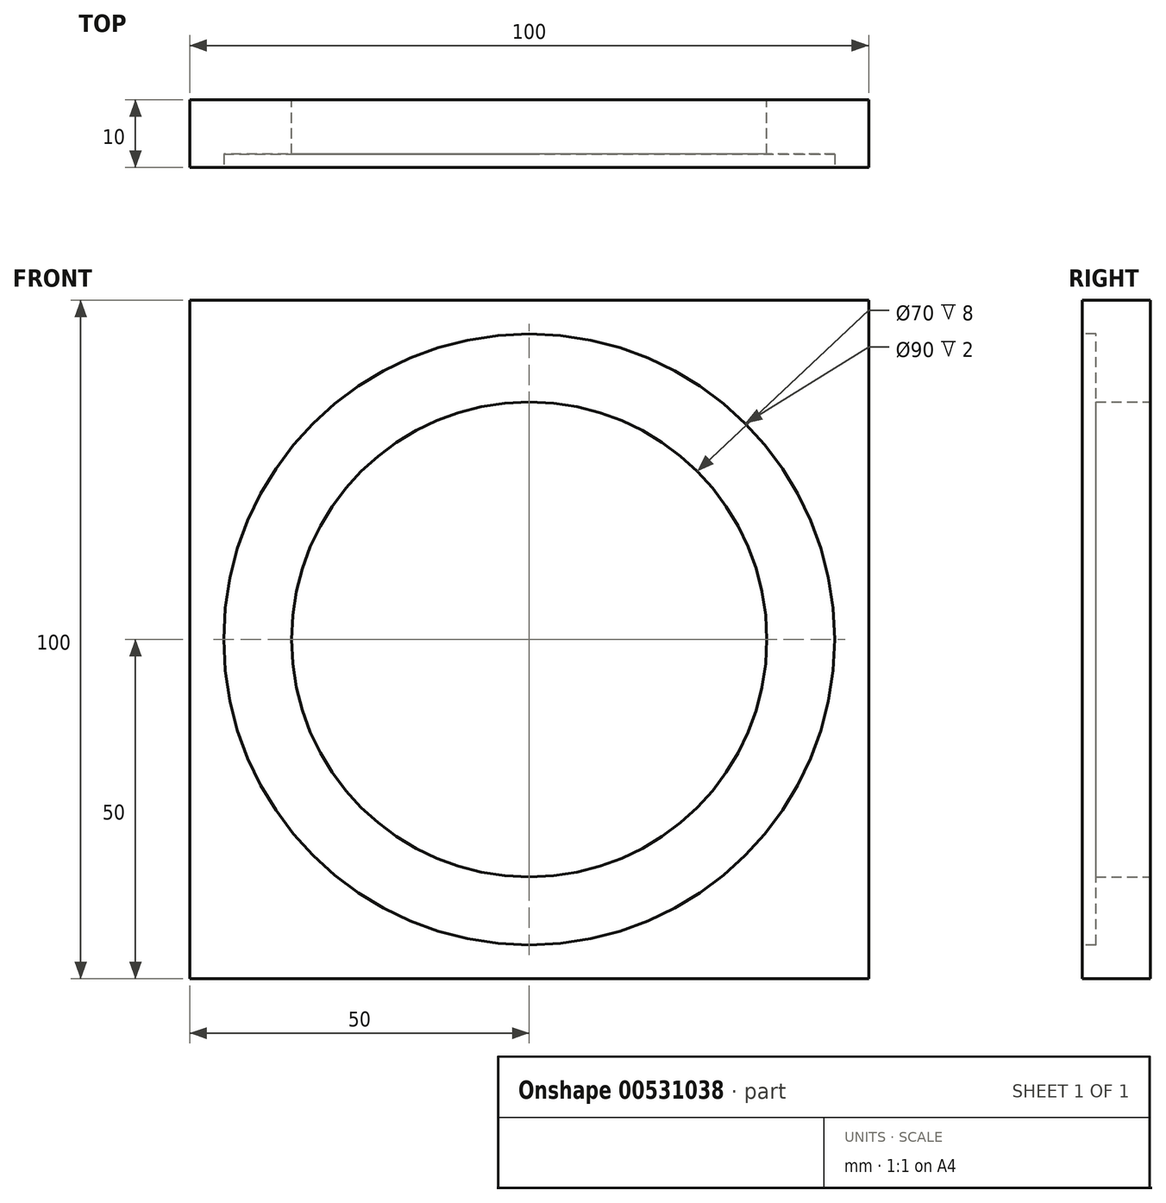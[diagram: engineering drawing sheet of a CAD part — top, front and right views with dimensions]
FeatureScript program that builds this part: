
annotation { "Feature Type Name" : "Feature", "Feature Type Description" : "" }
export const myFeature = defineFeature(function(context is Context, id is Id, definition is map)
    precondition{}
    {
        {
            var Q0;
            Q0=qCreatedBy(makeId("Front.planeOp"),FACE);
            var sketch = newSketch(context, id + "F0", { "sketchPlane" : qUnion([Q0])});
            skLineSegment(sketch, "E0.bottom", {"start": v(-50, -50) * mm, "end": v(50, -50) * mm});
            skLineSegment(sketch, "E0.top", {"start": v(-50, 50) * mm, "end": v(50, 50) * mm});
            skLineSegment(sketch, "E0.left", {"start": v(-50, -50) * mm, "end": v(-50, 50) * mm});
            skLineSegment(sketch, "E0.right", {"start": v(50, -50) * mm, "end": v(50, 50) * mm});
            skPoint(sketch, "E0.middle", {"position": v(0, 0) * mm});
            skCircle(sketch, "E1", {"center": v(0, 0) * mm, "radius": 35 * mm});
            skSolve(sketch);
        }
        {
            var Q0;
            Q0 = qSketchRegion(id + "F0", true);
            extrude(context, id + "F1", {"entities" : qUnion([Q0]), "depth" : 10 * mm, "offsetDistance" : 25 * mm});
        }
        {
            var Q0;
            Q0=makeQuery(id+"F1.opExtrude","CAP_FACE",FACE,{"disambiguationData":[OSD([sQuery(id+"F0.wireOp",EDGE,"E0.bottom"),sQuery(id+"F0.wireOp",EDGE,"E0.top"),sQuery(id+"F0.wireOp",EDGE,"E0.left"),sQuery(id+"F0.wireOp",EDGE,"E0.right"),sQuery(id+"F0.wireOp",EDGE,"E1")])],"isStart":false});
            var sketch = newSketch(context, id + "F2", { "sketchPlane" : qUnion([Q0])});
            skCircle(sketch, "E2", {"center": v(0, 0) * mm, "radius": 45 * mm});
            skSolve(sketch);
        }
        {
            var Q0;
            Q0 = qSketchRegion(id + "F2", true);
            extrude(context, id + "F3", {"entities" : qUnion([Q0]), "operationType" : NewBodyOperationType.REMOVE, "oppositeDirection" : true, "depth" : 2 * mm, "offsetDistance" : 25 * mm});
        }
    });
